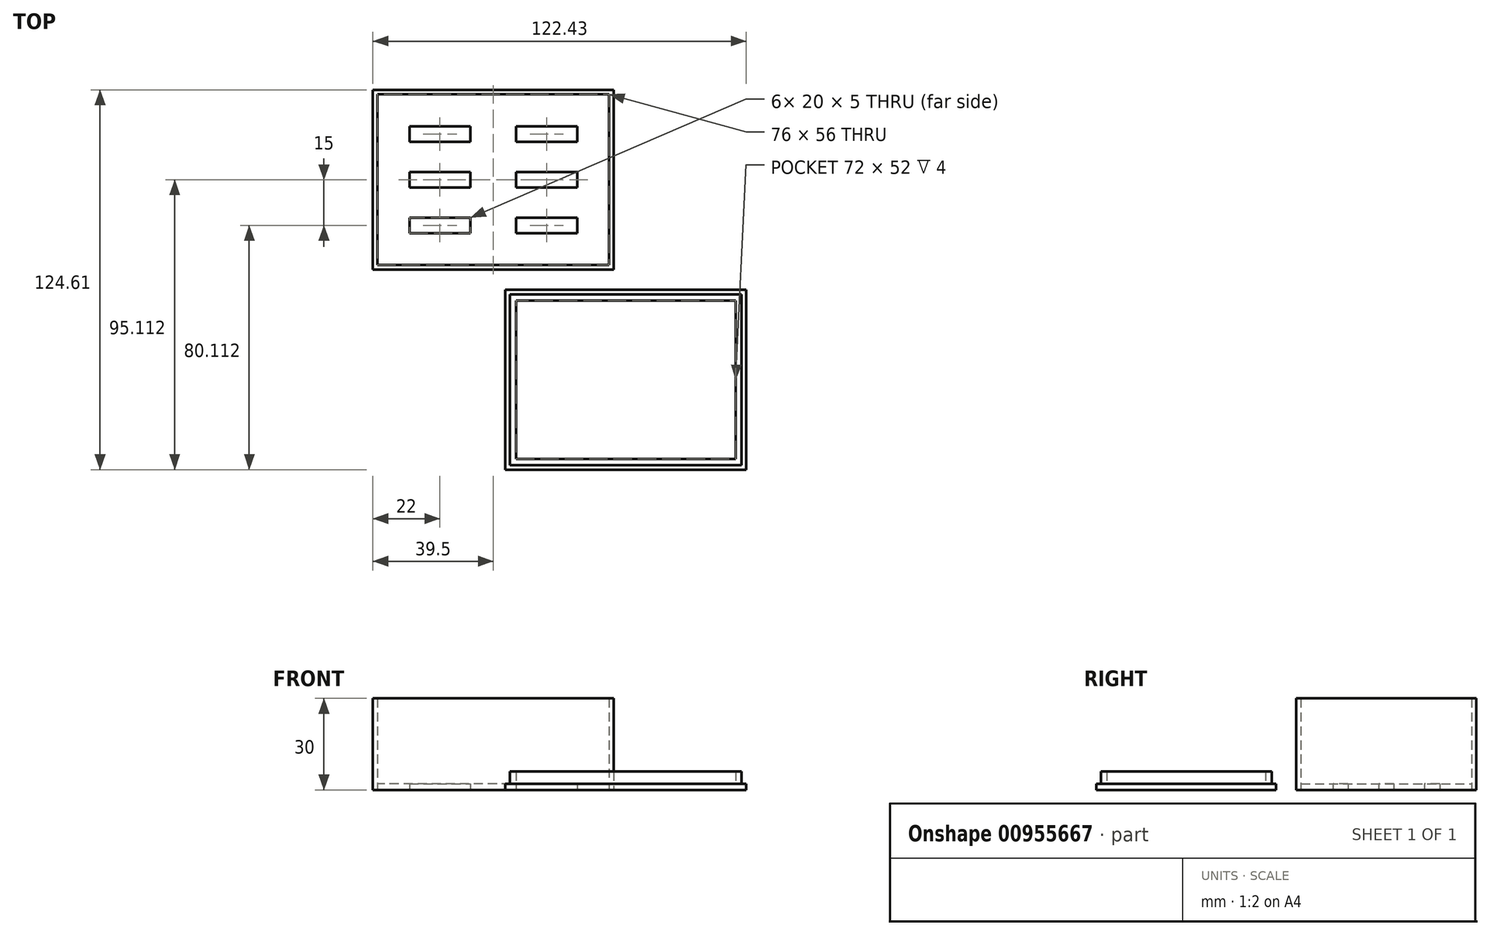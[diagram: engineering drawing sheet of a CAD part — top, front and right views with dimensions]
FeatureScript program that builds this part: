
annotation { "Feature Type Name" : "Feature", "Feature Type Description" : "" }
export const myFeature = defineFeature(function(context is Context, id is Id, definition is map)
    precondition{}
    {
        {
            var Q0;
            Q0=qCreatedBy(makeId("Top.planeOp"),FACE);
            var sketch = newSketch(context, id + "F0", { "sketchPlane" : qUnion([Q0])});
            skLineSegment(sketch, "E0.bottom", {"start": v(20.06, -2.62) * mm, "end": v(-58.94, -2.62) * mm});
            skLineSegment(sketch, "E0.top", {"start": v(20.06, 56.38) * mm, "end": v(-58.94, 56.38) * mm});
            skLineSegment(sketch, "E0.left", {"start": v(20.06, -2.62) * mm, "end": v(20.06, 56.38) * mm});
            skLineSegment(sketch, "E0.right", {"start": v(-58.94, -2.62) * mm, "end": v(-58.94, 56.38) * mm});
            skPoint(sketch, "E0.middle", {"position": v(5.66, 3.18) * mm});
            skLineSegment(sketch, "E1.bottom", {"start": v(-46.94, 44.38) * mm, "end": v(-26.94, 44.38) * mm});
            skLineSegment(sketch, "E1.top", {"start": v(-46.94, 39.38) * mm, "end": v(-26.94, 39.38) * mm});
            skLineSegment(sketch, "E1.left", {"start": v(-46.94, 44.38) * mm, "end": v(-46.94, 39.38) * mm});
            skLineSegment(sketch, "E1.right", {"start": v(-26.94, 44.38) * mm, "end": v(-26.94, 39.38) * mm});
            skLineSegment(sketch, "E2.bottom", {"start": v(-11.94, 44.38) * mm, "end": v(8.06, 44.38) * mm});
            skLineSegment(sketch, "E2.top", {"start": v(-11.94, 39.38) * mm, "end": v(8.06, 39.38) * mm});
            skLineSegment(sketch, "E2.left", {"start": v(-11.94, 44.38) * mm, "end": v(-11.94, 39.38) * mm});
            skLineSegment(sketch, "E2.right", {"start": v(8.06, 44.38) * mm, "end": v(8.06, 39.38) * mm});
            skLineSegment(sketch, "E3.bottom", {"start": v(-11.94, 14.38) * mm, "end": v(8.06, 14.38) * mm});
            skLineSegment(sketch, "E3.top", {"start": v(-11.94, 9.38) * mm, "end": v(8.06, 9.38) * mm});
            skLineSegment(sketch, "E3.left", {"start": v(-11.94, 14.38) * mm, "end": v(-11.94, 9.38) * mm});
            skLineSegment(sketch, "E3.right", {"start": v(8.06, 14.38) * mm, "end": v(8.06, 9.38) * mm});
            skLineSegment(sketch, "E4.bottom", {"start": v(-46.94, 14.38) * mm, "end": v(-26.94, 14.38) * mm});
            skLineSegment(sketch, "E4.top", {"start": v(-46.94, 9.38) * mm, "end": v(-26.94, 9.38) * mm});
            skLineSegment(sketch, "E4.left", {"start": v(-46.94, 14.38) * mm, "end": v(-46.94, 9.38) * mm});
            skLineSegment(sketch, "E4.right", {"start": v(-26.94, 14.38) * mm, "end": v(-26.94, 9.38) * mm});
            skLineSegment(sketch, "E5.bottom", {"start": v(-46.94, 29.38) * mm, "end": v(-26.94, 29.38) * mm});
            skLineSegment(sketch, "E5.top", {"start": v(-46.94, 24.38) * mm, "end": v(-26.94, 24.38) * mm});
            skLineSegment(sketch, "E5.left", {"start": v(-46.94, 29.38) * mm, "end": v(-46.94, 24.38) * mm});
            skLineSegment(sketch, "E5.right", {"start": v(-26.94, 29.38) * mm, "end": v(-26.94, 24.38) * mm});
            skLineSegment(sketch, "E6.bottom", {"start": v(-11.94, 29.38) * mm, "end": v(8.06, 29.38) * mm});
            skLineSegment(sketch, "E6.top", {"start": v(-11.94, 24.38) * mm, "end": v(8.06, 24.38) * mm});
            skLineSegment(sketch, "E6.left", {"start": v(-11.94, 29.38) * mm, "end": v(-11.94, 24.38) * mm});
            skLineSegment(sketch, "E6.right", {"start": v(8.06, 29.38) * mm, "end": v(8.06, 24.38) * mm});
            skLineSegment(sketch, "E7.bottom", {"start": v(18.56, -1.12) * mm, "end": v(-57.44, -1.12) * mm});
            skLineSegment(sketch, "E7.top", {"start": v(18.56, 54.88) * mm, "end": v(-57.44, 54.88) * mm});
            skLineSegment(sketch, "E7.left", {"start": v(18.56, -1.12) * mm, "end": v(18.56, 54.88) * mm});
            skLineSegment(sketch, "E7.right", {"start": v(-57.44, -1.12) * mm, "end": v(-57.44, 54.88) * mm});
            skSolve(sketch);
        }
        {
            var Q0;
            Q0=makeQuery(id+"F0.imprint","IMPRINT",FACE,{"disambiguationData":[TD([[makeQuery(id+"F0.imprint","IMPRINT",EDGE,{"derivedFrom":sQuery(id+"F0.wireOp",EDGE,"E1.bottom")}),1.0]])]});
            extrude(context, id + "F1", {"entities" : qUnion([Q0]), "oppositeDirection" : true, "depth" : 0 * mm, "offsetDistance" : 25 * mm, "hasSecondDirection" : true, "secondDirectionOppositeDirection" : false, "secondDirectionDepth" : 2 * mm});
        }
        {
            var Q0;
            Q0=qCreatedBy(makeId("Top.planeOp"),FACE);
            var sketch = newSketch(context, id + "F2", { "sketchPlane" : qUnion([Q0])});
            skLineSegment(sketch, "E8.bottom", {"start": v(-15.51, -68.23) * mm, "end": v(63.49, -68.23) * mm});
            skLineSegment(sketch, "E8.top", {"start": v(-15.51, -9.23) * mm, "end": v(63.49, -9.23) * mm});
            skLineSegment(sketch, "E8.left", {"start": v(-15.51, -68.23) * mm, "end": v(-15.51, -9.23) * mm});
            skLineSegment(sketch, "E8.right", {"start": v(63.49, -68.23) * mm, "end": v(63.49, -9.23) * mm});
            skPoint(sketch, "E8.middle", {"position": v(23.99, -38.73) * mm});
            skLineSegment(sketch, "E9.bottom", {"start": v(-14.01, -10.73) * mm, "end": v(61.99, -10.73) * mm});
            skLineSegment(sketch, "E9.top", {"start": v(-14.01, -66.73) * mm, "end": v(61.99, -66.73) * mm});
            skLineSegment(sketch, "E9.left", {"start": v(-14.01, -10.73) * mm, "end": v(-14.01, -66.73) * mm});
            skLineSegment(sketch, "E9.right", {"start": v(61.99, -10.73) * mm, "end": v(61.99, -66.73) * mm});
            skLineSegment(sketch, "E10.bottom", {"start": v(-12.01, -12.73) * mm, "end": v(59.99, -12.73) * mm});
            skLineSegment(sketch, "E10.top", {"start": v(-12.01, -64.73) * mm, "end": v(59.99, -64.73) * mm});
            skLineSegment(sketch, "E10.left", {"start": v(-12.01, -12.73) * mm, "end": v(-12.01, -64.73) * mm});
            skLineSegment(sketch, "E10.right", {"start": v(59.99, -12.73) * mm, "end": v(59.99, -64.73) * mm});
            skSolve(sketch);
        }
        {
            var Q0;
            Q0=makeQuery(id+"F2.imprint","IMPRINT",FACE,{"disambiguationData":[TD([[makeQuery(id+"F2.imprint","IMPRINT",EDGE,{"derivedFrom":sQuery(id+"F2.wireOp",EDGE,"E9.bottom")}),-1.0]])]});
            extrude(context, id + "F3", {"entities" : qUnion([Q0]), "depth" : 4 * mm, "offsetDistance" : 25 * mm});
        }
        {
            var Q0;
            Q0=makeQuery(id+"F2.imprint","IMPRINT",FACE,{"disambiguationData":[TD([[makeQuery(id+"F2.imprint","IMPRINT",EDGE,{"derivedFrom":sQuery(id+"F2.wireOp",EDGE,"E8.bottom")}),1.0]])]});
            var Q1;
            Q1=makeQuery(id+"F2.imprint","IMPRINT",FACE,{"disambiguationData":[TD([[makeQuery(id+"F2.imprint","IMPRINT",EDGE,{"derivedFrom":sQuery(id+"F2.wireOp",EDGE,"E9.bottom")}),-1.0]])]});
            var Q2;
            Q2=makeQuery(id+"F2.imprint","IMPRINT",FACE,{"disambiguationData":[TD([[makeQuery(id+"F2.imprint","IMPRINT",EDGE,{"derivedFrom":sQuery(id+"F2.wireOp",EDGE,"E10.bottom")}),-1.0]])]});
            var Q3;
            Q3=makeQuery(id+"F3.opExtrude","CAP_FACE",FACE,{"disambiguationData":[OSD([sQuery(id+"F2.wireOp",EDGE,"E9.bottom"),sQuery(id+"F2.wireOp",EDGE,"E9.top"),sQuery(id+"F2.wireOp",EDGE,"E9.left"),sQuery(id+"F2.wireOp",EDGE,"E9.right"),sQuery(id+"F2.wireOp",EDGE,"E10.bottom"),sQuery(id+"F2.wireOp",EDGE,"E10.top"),sQuery(id+"F2.wireOp",EDGE,"E10.left"),sQuery(id+"F2.wireOp",EDGE,"E10.right")])],"isStart":false});
            extrude(context, id + "F4", {"entities" : qUnion([Q0, Q1, Q2, Q3]), "operationType" : NewBodyOperationType.ADD, "depth" : 2 * mm, "offsetDistance" : 25 * mm});
        }
        {
            var Q0;
            Q0=makeQuery(id+"F0.imprint","IMPRINT",FACE,{"disambiguationData":[TD([[makeQuery(id+"F0.imprint","IMPRINT",EDGE,{"derivedFrom":sQuery(id+"F0.wireOp",EDGE,"E0.bottom")}),-1.0]])]});
            extrude(context, id + "F5", {"entities" : qUnion([Q0]), "depth" : 30 * mm, "offsetDistance" : 25 * mm, "hasSecondDirection" : true, "secondDirectionOppositeDirection" : true, "secondDirectionDepth" : 0 * mm});
        }
    });
